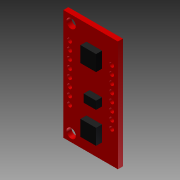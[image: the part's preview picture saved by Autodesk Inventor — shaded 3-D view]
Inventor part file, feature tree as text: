
AUTODESK INVENTOR PART (.ipt)
format: ipt  version: 2012 (Build 160160000, 160)  size: 223,744 bytes
history: native  units: in
note: dims shown in document units (in); Inventor stores cm internally (conversion verified against a paired STEP export)
features: extrude x2, sketch x1, fillet x1
ambient origin geometry x8: Origin, YZ Plane, XZ Plane, XY Plane, X Axis, Y Axis, Z Axis, Center Point
bodies: Solid1 (feature_tree)
feature tree (4):
  sketch  "Sketch1"  dims[d0=3.2283in d1=2.1654in d2=0.689in d3=1.3976in d4=0.4528in d5=0.0984in d6=0.0394in d7=0.3937in d8=1.0825in d9=0.3543in d10=0.3937in d11=0.2362in d12=0.9in d13=0.7569in d14=0.1in d15=0.027in d16=0.3937in d17=0.1in d18=0.02in d19=0.177in d20=0.177in d21=0.1in d22=0.177in d23=0.02in d24=0.1181in d25=0.0591in d26=0.2953in d27=0.0787in d28=0.0591in d29=0.0591in d30=0.0591in d31=0.0591in d32=0.0591in d33=0.0591in d34=0.0591in d35=0.1in d36=0.1in d37=0.1in d38=0.1in d39=0.1in d40=0.1in d41=0.1in d42=0.0591in d43=0.0591in d44=0.0591in d45=0.0591in d46=0.0591in d47=0.0591in d48=0.0591in d49=0.0591in d50=0.1in d51=0.1in d52=0.1in d53=0.1in d54=0.1in d55=0.1in d56=0.1in d57=0.0787in d58=0.2953in d59=0.0787in d60=0.0787in d61=0.0787in d62=0.0787in d63=0.0787in d64=0.0787in d65=0.0787in d66=0.1969in d67=0.1969in d68=0.1969in d69=0.1969in d70=0.0591in d71=0.0591in d72=0.1969in d73=0.1969in d74=0.0591in d75=0.0591in d76=0.0787in d77=0.0787in d78=0.1969in d79=0.1969in d80=0.1in d81=0.1in d82=0.1969in d83=0.1969in d84=0.1575in d85=0.1in d86=0.1969in d87=0.1969in d88=0.1969in d89=0.1969in d90=0.1969in d91=0.1969in d92=0.1969in d93=0.1969in d94=0.1181in d95=0.1181in d96=0.0394in d97=0.0394in d98=0.0394in d99=0.0394in d100=0.0787in d101=0.0in d102=0.005in d103=0.063in d104=0.0in]
  extrude  "Extrusion1"  Depth=0.0787in TaperAngle=0.0deg
  fillet  "Fillet1"  Radius=0.005in
  extrude  "Extrusion2"  Depth=0.063in TaperAngle=0.0deg
